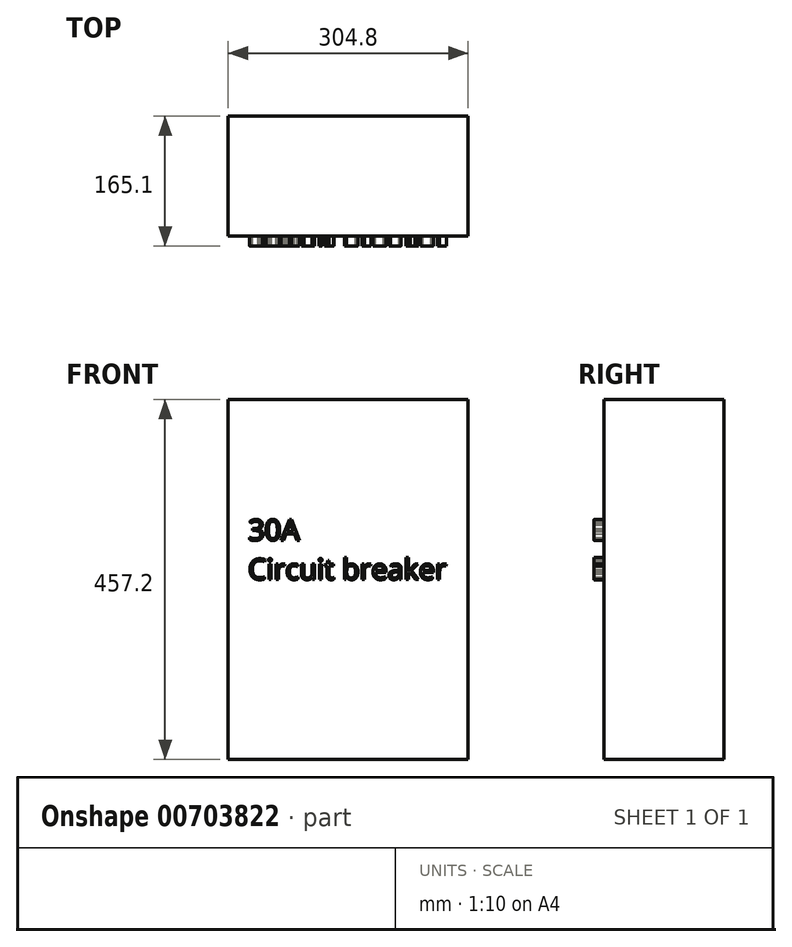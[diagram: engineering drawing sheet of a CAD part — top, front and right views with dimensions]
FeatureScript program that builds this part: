
annotation { "Feature Type Name" : "Feature", "Feature Type Description" : "" }
export const myFeature = defineFeature(function(context is Context, id is Id, definition is map)
    precondition{}
    {
        {
            var Q0;
            Q0=qCreatedBy(makeId("Front.planeOp"),FACE);
            var sketch = newSketch(context, id + "F0", { "sketchPlane" : qUnion([Q0])});
            skLineSegment(sketch, "E0.bottom", {"start": v(152.4, -228.6) * mm, "end": v(-152.4, -228.6) * mm});
            skLineSegment(sketch, "E0.top", {"start": v(152.4, 228.6) * mm, "end": v(-152.4, 228.6) * mm});
            skLineSegment(sketch, "E0.left", {"start": v(152.4, -228.6) * mm, "end": v(152.4, 228.6) * mm});
            skLineSegment(sketch, "E0.right", {"start": v(-152.4, -228.6) * mm, "end": v(-152.4, 228.6) * mm});
            skPoint(sketch, "E0.middle", {"position": v(0, 0) * mm});
            skSolve(sketch);
        }
        {
            var Q0;
            Q0=makeQuery(id+"F0.imprint","IMPRINT",FACE,{"disambiguationData":[TD([[makeQuery(id+"F0.imprint","IMPRINT",EDGE,{"derivedFrom":sQuery(id+"F0.wireOp",EDGE,"E0.bottom")}),-1.0]])]});
            extrude(context, id + "F1", {"entities" : qUnion([Q0]), "depth" : 152.4 * mm, "offsetDistance" : 25.4 * mm});
        }
        {
            var Q0;
            Q0=makeQuery(id+"F1.opExtrude","CAP_FACE",FACE,{"disambiguationData":[OSD([sQuery(id+"F0.wireOp",EDGE,"E0.bottom"),sQuery(id+"F0.wireOp",EDGE,"E0.top"),sQuery(id+"F0.wireOp",EDGE,"E0.left"),sQuery(id+"F0.wireOp",EDGE,"E0.right")])],"isStart":false});
            var sketch = newSketch(context, id + "F2", { "sketchPlane" : qUnion([Q0])});
            skText(sketch, "E1", { "text": "30A \nCircuit breaker\n", "fontName": "OpenSans-Regular.ttf"});
            const initialGuessF2  = {"E1": [-0.127, 0.04981, 1, 0, 0.02639]};
            skSetInitialGuess(sketch, initialGuessF2);
            skSolve(sketch);
        }
        {
            var Q0;
            Q0 = qSketchRegion(id + "F2", true);
            extrude(context, id + "F3", {"entities" : qUnion([Q0]), "operationType" : NewBodyOperationType.ADD, "depth" : 12.7 * mm, "offsetDistance" : 25.4 * mm});
        }
    });
